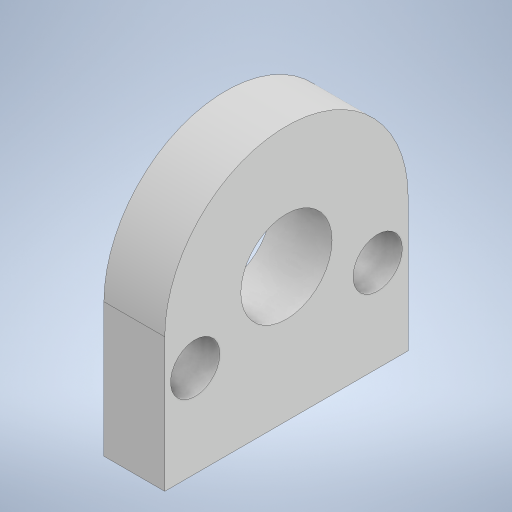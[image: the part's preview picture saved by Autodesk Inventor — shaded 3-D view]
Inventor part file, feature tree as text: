
AUTODESK INVENTOR PART (.ipt)
format: ipt  version: 2023.2 (Build 272271030, 271C)  size: 233,984 bytes
history: native  units: mm
features: extrude x2, sketch x2, projected_geometry x1
ambient origin geometry x8: Origin, YZ Plane, XZ Plane, XY Plane, X Axis, Y Axis, Z Axis, Center Point
bodies: Solid1 (feature_tree)
feature tree (5):
  extrude  "Extrusion1"  Depth=22.0mm
  extrude  "Extrusion2"  Depth=10.0mm
  sketch  "Sketch1"  dims[d0=22.0mm d1=22.0mm]
  sketch  "Sketch2"  dims[d2=40.0mm d3=15.0mm d4=10.0mm d5=0.0mm d6=15.05mm d7=8.1mm d8=5.0mm d9=0.0mm d10=0.0mm]
  projected_geometry  "Projected Loop1"
